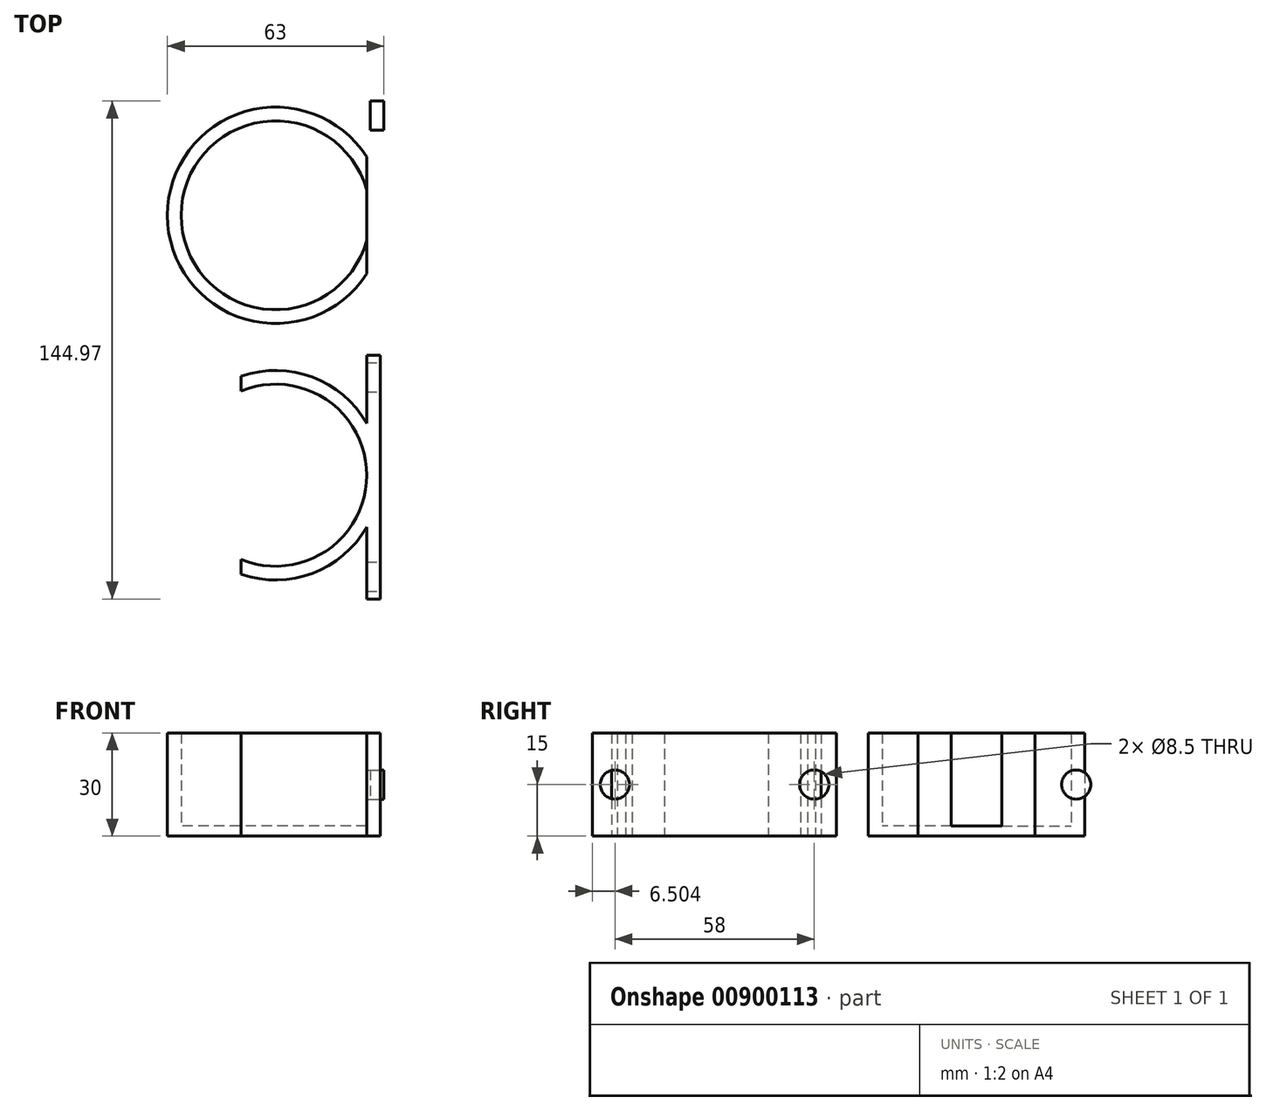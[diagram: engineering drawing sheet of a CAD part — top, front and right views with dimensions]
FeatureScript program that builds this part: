
annotation { "Feature Type Name" : "Feature", "Feature Type Description" : "" }
export const myFeature = defineFeature(function(context is Context, id is Id, definition is map)
    precondition{}
    {
        {
            var Q0;
            Q0=qCreatedBy(makeId("Top.planeOp"),FACE);
            var sketch = newSketch(context, id + "F0", { "sketchPlane" : qUnion([Q0])});
            skCircle(sketch, "E0", {"center": v(0, 0) * mm, "radius": 27.5 * mm});
            skCircle(sketch, "E1.0", {"center": v(0, 0) * mm, "radius": 31.5 * mm});
            skSolve(sketch);
        }
        {
            var Q0;
            Q0=makeQuery(id+"F0.imprint","IMPRINT",FACE,{"disambiguationData":[TD([[makeQuery(id+"F0.imprint","IMPRINT",EDGE,{"derivedFrom":sQuery(id+"F0.wireOp",EDGE,"E0")}),-1.0]])]});
            extrude(context, id + "F1", {"entities" : qUnion([Q0]), "depth" : 30 * mm, "offsetDistance" : 25 * mm});
        }
        {
            var Q0;
            Q0=makeQuery(id+"F1.opExtrude","CAP_FACE",FACE,{"disambiguationData":[OSD([sQuery(id+"F0.wireOp",EDGE,"E0"),sQuery(id+"F0.wireOp",EDGE,"E1.0")])],"isStart":true});
            var sketch = newSketch(context, id + "F2", { "sketchPlane" : qUnion([Q0])});
            skCircle(sketch, "E2", {"center": v(0, 0) * mm, "radius": 31.5 * mm});
            skSolve(sketch);
        }
        {
            var Q0;
            Q0=makeQuery(id+"F2.imprint","IMPRINT",FACE,{"disambiguationData":[TD([[makeQuery(id+"F2.imprint","IMPRINT",EDGE,{"derivedFrom":makeQuery(id+"F1.opExtrude","CAP_EDGE",EDGE,{"disambiguationData":[OSD([sQuery(id+"F0.wireOp",EDGE,"E0")])],"isStart":true})}),-1.0]])]});
            var Q1;
            Q1=makeQuery(id+"F2.imprint","IMPRINT",FACE,{"disambiguationData":[TD([[makeQuery(id+"F2.imprint","IMPRINT",EDGE,{"derivedFrom":sQuery(id+"F2.wireOp",EDGE,"E2")}),-1.0]])]});
            extrude(context, id + "F3", {"entities" : qUnion([Q0, Q1]), "operationType" : NewBodyOperationType.ADD, "oppositeDirection" : true, "depth" : 3 * mm, "offsetDistance" : 25 * mm});
        }
        {
            var Q0;
            Q0=makeQuery(id+"F1.opExtrude","CAP_FACE",FACE,{"disambiguationData":[OSD([sQuery(id+"F0.wireOp",EDGE,"E0"),sQuery(id+"F0.wireOp",EDGE,"E1.0")])],"isStart":false});
            var sketch = newSketch(context, id + "F4", { "sketchPlane" : qUnion([Q0])});
            skLineSegment(sketch, "E3", {"start": v(27.5, 0) * mm, "end": v(27.5, -35.5) * mm});
            skLineSegment(sketch, "E4", {"start": v(27.5, -35.5) * mm, "end": v(31.5, -35.5) * mm});
            skLineSegment(sketch, "E5", {"start": v(31.5, -35.5) * mm, "end": v(31.5, 35.5) * mm});
            skLineSegment(sketch, "E6", {"start": v(31.5, 35.5) * mm, "end": v(27.5, 35.5) * mm});
            skLineSegment(sketch, "E7", {"start": v(27.5, 35.5) * mm, "end": v(27.5, 0) * mm});
            skSolve(sketch);
        }
        {
            var Q0;
            {var subQ0=sQuery(id+"F4.wireOp",EDGE,"E6");Q0=makeQuery(id+"F4.imprint","IMPRINT",FACE,{"disambiguationData":[TD([[makeQuery(id+"F4.imprint","IMPRINT",EDGE,{"derivedFrom":subQ0}),1.0]])]});}
            var Q1;
            {var subQ0=sQuery(id+"F4.wireOp",EDGE,"E4");Q1=makeQuery(id+"F4.imprint","IMPRINT",FACE,{"disambiguationData":[TD([[makeQuery(id+"F4.imprint","IMPRINT",EDGE,{"derivedFrom":subQ0}),1.0]])]});}
            extrude(context, id + "F5", {"entities" : qUnion([Q0, Q1]), "operationType" : NewBodyOperationType.ADD, "oppositeDirection" : true, "depth" : 30 * mm, "offsetDistance" : 25 * mm});
        }
        {
            var Q0;
            {var subQ0=sQuery(id+"F4.wireOp",EDGE,"E5");Q0=makeQuery(id+"F5.boolean.opBoolean","MERGE",FACE,{"derivedFrom":[makeQuery(id+"F5.opExtrude","SWEPT_FACE",FACE,{"disambiguationData":[OSD([subQ0]),TDD([makeQuery(id+"F4.imprint","IMPRINT",EDGE,{"disambiguationData":[TD([[makeQuery(id+"F4.imprint","INTERSECT",VERTEX,{"derivedFrom":[sQuery(id+"F4.wireOp",EDGE,"E4"),subQ0]}),-1.0]])],"derivedFrom":subQ0})])]}),makeQuery(id+"F5.opExtrude","SWEPT_FACE",FACE,{"disambiguationData":[OSD([subQ0]),TDD([makeQuery(id+"F4.imprint","IMPRINT",EDGE,{"disambiguationData":[TD([[makeQuery(id+"F4.imprint","INTERSECT",VERTEX,{"derivedFrom":[subQ0,sQuery(id+"F4.wireOp",EDGE,"E6")]}),1.0]])],"derivedFrom":subQ0})])]})]});}
            var sketch = newSketch(context, id + "F6", { "sketchPlane" : qUnion([Q0])});
            skCircle(sketch, "E8", {"center": v(-29, 15) * mm, "radius": 4.25 * mm});
            skPoint(sketch, "E8.centerSnap0", {"position": v(-35.5, 15) * mm});
            skCircle(sketch, "E9.MirrorC", {"center": v(29, 15) * mm, "radius": 4.25 * mm});
            skSolve(sketch);
        }
        {
            var Q0;
            Q0=makeQuery(id+"F6.imprint","IMPRINT",FACE,{"disambiguationData":[TD([[makeQuery(id+"F6.imprint","IMPRINT",EDGE,{"derivedFrom":sQuery(id+"F6.wireOp",EDGE,"E9.MirrorC")}),-1.0]])]});
            var Q1;
            Q1=makeQuery(id+"F6.imprint","IMPRINT",FACE,{"disambiguationData":[TD([[makeQuery(id+"F6.imprint","IMPRINT",EDGE,{"derivedFrom":sQuery(id+"F6.wireOp",EDGE,"E8")}),1.0]])]});
            extrude(context, id + "F7", {"entities" : qUnion([Q0, Q1]), "operationType" : NewBodyOperationType.REMOVE, "oppositeDirection" : true, "depth" : 5 * mm, "offsetDistance" : 25 * mm});
        }
        {
            var Q0;
            Q0=qCreatedBy(makeId("Top.planeOp"),FACE);
            var sketch = newSketch(context, id + "F8", { "sketchPlane" : qUnion([Q0])});
            skCircle(sketch, "E10", {"center": v(0, -75.66) * mm, "radius": 26.5 * mm});
            skCircle(sketch, "E11.0", {"center": v(0, -75.66) * mm, "radius": 30.5 * mm});
            skLineSegment(sketch, "E12", {"start": v(-10, -46.85) * mm, "end": v(-10, -51.12) * mm});
            skLineSegment(sketch, "E13.trimOffspring", {"start": v(-10, -100.2) * mm, "end": v(-10, -104.48) * mm});
            skLineSegment(sketch, "E14", {"start": v(26.5, -76.22) * mm, "end": v(26.5, -40.72) * mm});
            skLineSegment(sketch, "E15", {"start": v(26.5, -40.72) * mm, "end": v(30.5, -40.72) * mm});
            skLineSegment(sketch, "E16", {"start": v(30.5, -40.72) * mm, "end": v(30.5, -111.72) * mm});
            skLineSegment(sketch, "E17", {"start": v(26.5, -40.72) * mm, "end": v(26.5, -111.72) * mm});
            skLineSegment(sketch, "E18", {"start": v(26.5, -111.72) * mm, "end": v(30.5, -111.72) * mm});
            skSolve(sketch);
        }
        {
            var Q0;
            {var subQ5=sQuery(id+"F8.wireOp",EDGE,"PAtGaIM8-xm5Z-fBkq-NVdI-j6WzneUi0y8M");Q0=makeQuery(id+"F8.imprint","IMPRINT",FACE,{"disambiguationData":[TD([[makeQuery(id+"F8.imprint","IMPRINT",EDGE,{"derivedFrom":subQ5}),1.0]])]});}
            var Q1;
            {var subQ5=sQuery(id+"F8.wireOp",EDGE,"7yM3ToNX-IIhT-RYkj-6QdW-8gnqzTuD2qfo");Q1=makeQuery(id+"F8.imprint","IMPRINT",FACE,{"disambiguationData":[TD([[makeQuery(id+"F8.imprint","IMPRINT",EDGE,{"derivedFrom":subQ5}),1.0]])]});}
            var Q2;
            {var subQ0=sQuery(id+"F8.wireOp",EDGE,"E13.trimOffspring");Q2=makeQuery(id+"F8.imprint","IMPRINT",FACE,{"disambiguationData":[TD([[makeQuery(id+"F8.imprint","IMPRINT",EDGE,{"derivedFrom":subQ0}),1.0]])]});}
            var Q3;
            {var subQ0=sQuery(id+"F8.wireOp",EDGE,"E12");Q3=makeQuery(id+"F8.imprint","IMPRINT",FACE,{"disambiguationData":[TD([[makeQuery(id+"F8.imprint","IMPRINT",EDGE,{"derivedFrom":subQ0}),1.0]])]});}
            var Q4;
            {var subQ0=sQuery(id+"F8.wireOp",EDGE,"EVq81sSU-csSB-STTn-lDz7-I4BDQVvBDS50");var subQ1=sQuery(id+"F8.wireOp",EDGE,"E11.0");var subQ2=makeQuery(id+"F8.imprint","INTERSECT",VERTEX,{"disambiguationData":[OD(0.0)],"derivedFrom":[subQ1,subQ0]});Q4=makeQuery(id+"F8.imprint","IMPRINT",FACE,{"disambiguationData":[TD([[makeQuery(id+"F8.imprint","IMPRINT",EDGE,{"disambiguationData":[TD([[subQ2,-1.0]])],"derivedFrom":subQ1}),1.0]])]});}
            var Q5;
            {var subQ5=sQuery(id+"F8.wireOp",EDGE,"pTQ2HIhw-Uaio-OcFA-twjG-LKvVv4lDPjvm");Q5=makeQuery(id+"F8.imprint","IMPRINT",FACE,{"disambiguationData":[TD([[makeQuery(id+"F8.imprint","IMPRINT",EDGE,{"derivedFrom":subQ5}),1.0]])]});}
            var Q6;
            {var subQ5=sQuery(id+"F8.wireOp",EDGE,"M0GYMIlv-OzGc-j3BZ-hZtM-BrqhB7Xa0YUN");Q6=makeQuery(id+"F8.imprint","IMPRINT",FACE,{"disambiguationData":[TD([[makeQuery(id+"F8.imprint","IMPRINT",EDGE,{"derivedFrom":subQ5}),1.0]])]});}
            var Q7;
            {var subQ5=sQuery(id+"F8.wireOp",EDGE,"E18");Q7=makeQuery(id+"F8.imprint","IMPRINT",FACE,{"disambiguationData":[TD([[makeQuery(id+"F8.imprint","IMPRINT",EDGE,{"derivedFrom":subQ5}),1.0]])]});}
            var Q8;
            {var subQ0=sQuery(id+"F8.wireOp",EDGE,"E17");var subQ1=makeQuery(id+"F8.imprint","IMPRINT",VERTEX,{"derivedFrom":subQ0});Q8=makeQuery(id+"F8.imprint","IMPRINT",FACE,{"disambiguationData":[TD([[makeQuery(id+"F8.imprint","IMPRINT",EDGE,{"disambiguationData":[TD([[subQ1,1.0]])],"derivedFrom":subQ0}),1.0]])]});}
            var Q9;
            {var subQ5=sQuery(id+"F8.wireOp",EDGE,"E15");Q9=makeQuery(id+"F8.imprint","IMPRINT",FACE,{"disambiguationData":[TD([[makeQuery(id+"F8.imprint","IMPRINT",EDGE,{"derivedFrom":subQ5}),-1.0]])]});}
            extrude(context, id + "F9", {"entities" : qUnion([Q0, Q1, Q2, Q3, Q4, Q5, Q6, Q7, Q8, Q9]), "depth" : 30 * mm, "offsetDistance" : 25 * mm});
        }
        {
            var Q0;
            Q0=makeQuery(id+"F9.opExtrude","SWEPT_FACE",FACE,{"disambiguationData":[OSD([sQuery(id+"F8.wireOp",EDGE,"E16")])]});
            var sketch = newSketch(context, id + "F10", { "sketchPlane" : qUnion([Q0])});
            skCircle(sketch, "E19", {"center": v(-47.22, 15) * mm, "radius": 4.25 * mm});
            skPoint(sketch, "E19.centerSnap0", {"position": v(-40.72, 15) * mm});
            skCircle(sketch, "E20", {"center": v(-105.22, 15) * mm, "radius": 4.25 * mm});
            skSolve(sketch);
        }
        {
            var Q0;
            Q0=makeQuery(id+"F10.imprint","IMPRINT",FACE,{"disambiguationData":[TD([[makeQuery(id+"F10.imprint","IMPRINT",EDGE,{"derivedFrom":sQuery(id+"F10.wireOp",EDGE,"E20")}),1.0]])]});
            var Q1;
            Q1=makeQuery(id+"F10.imprint","IMPRINT",FACE,{"disambiguationData":[TD([[makeQuery(id+"F10.imprint","IMPRINT",EDGE,{"derivedFrom":sQuery(id+"F10.wireOp",EDGE,"E19")}),1.0]])]});
            extrude(context, id + "F11", {"entities" : qUnion([Q0, Q1]), "operationType" : NewBodyOperationType.REMOVE, "oppositeDirection" : true, "depth" : 5 * mm, "offsetDistance" : 25 * mm});
        }
    });
